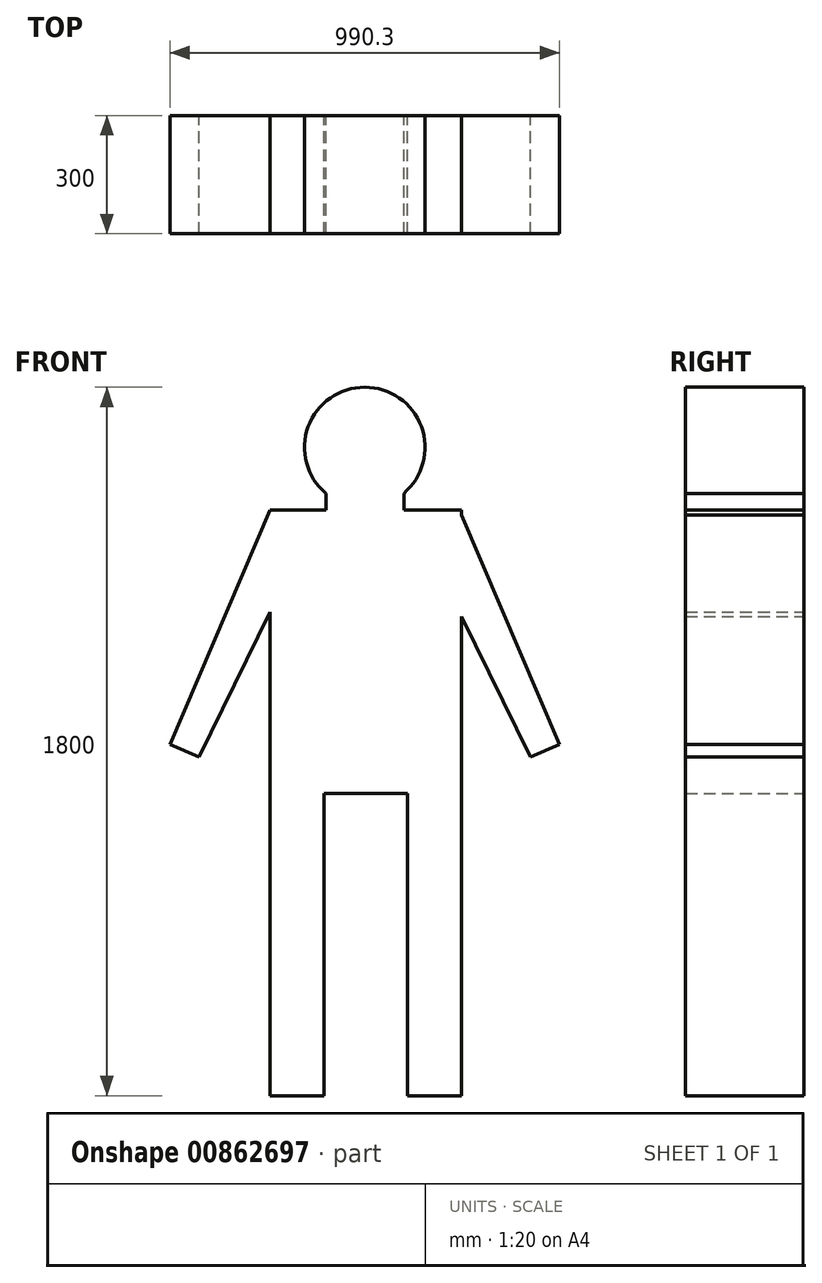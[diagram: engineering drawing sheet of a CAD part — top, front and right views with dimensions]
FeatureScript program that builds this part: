
annotation { "Feature Type Name" : "Feature", "Feature Type Description" : "" }
export const myFeature = defineFeature(function(context is Context, id is Id, definition is map)
    precondition{}
    {
        {
            var Q0;
            Q0=qCreatedBy(makeId("Front.planeOp"),FACE);
            var sketch = newSketch(context, id + "F0", { "sketchPlane" : qUnion([Q0])});
            skCircle(sketch, "E0", {"center": v(0, 754.64) * mm, "radius": 153.03 * mm});
            skLineSegment(sketch, "E1.bottom", {"start": v(-240.95, 595.77) * mm, "end": v(246.25, 595.77) * mm});
            skLineSegment(sketch, "E1.top", {"start": v(-240.95, -124.45) * mm, "end": v(246.25, -124.45) * mm});
            skLineSegment(sketch, "E1.left", {"start": v(-240.95, 595.77) * mm, "end": v(-240.95, -124.45) * mm});
            skLineSegment(sketch, "E1.right", {"start": v(246.25, 595.77) * mm, "end": v(246.25, -124.45) * mm});
            skLineSegment(sketch, "E2.bottom", {"start": v(-240.95, -124.45) * mm, "end": v(-103.27, -124.45) * mm});
            skLineSegment(sketch, "E2.top", {"start": v(-240.95, -892.33) * mm, "end": v(-103.27, -892.33) * mm});
            skLineSegment(sketch, "E2.left", {"start": v(-240.95, -124.45) * mm, "end": v(-240.95, -892.33) * mm});
            skLineSegment(sketch, "E2.right", {"start": v(-103.27, -124.45) * mm, "end": v(-103.27, -892.33) * mm});
            skLineSegment(sketch, "E3.bottom", {"start": v(108.56, -124.45) * mm, "end": v(246.25, -124.45) * mm});
            skLineSegment(sketch, "E3.top", {"start": v(108.56, -892.33) * mm, "end": v(246.25, -892.33) * mm});
            skLineSegment(sketch, "E3.left", {"start": v(108.56, -124.45) * mm, "end": v(108.56, -892.33) * mm});
            skLineSegment(sketch, "E3.right", {"start": v(246.25, -124.45) * mm, "end": v(246.25, -892.33) * mm});
            skLineSegment(sketch, "E4", {"start": v(-240.95, 595.77) * mm, "end": v(-495.15, 0) * mm});
            skLineSegment(sketch, "E5", {"start": v(-495.15, 0) * mm, "end": v(-421.26, -31.53) * mm});
            skLineSegment(sketch, "E6", {"start": v(-421.26, -31.53) * mm, "end": v(-240.95, 336.28) * mm});
            skLineSegment(sketch, "E7.MirrorCS", {"start": v(421.26, -31.53) * mm, "end": v(240.95, 336.28) * mm});
            skLineSegment(sketch, "E8.MirrorCS", {"start": v(240.95, 595.77) * mm, "end": v(495.15, 0) * mm});
            skLineSegment(sketch, "E9.MirrorCS", {"start": v(495.15, 0) * mm, "end": v(421.26, -31.53) * mm});
            skLineSegment(sketch, "E10", {"start": v(-99.07, 638) * mm, "end": v(-99.07, 595.77) * mm});
            skLineSegment(sketch, "E11.MirrorCS", {"start": v(99.07, 638) * mm, "end": v(99.07, 595.77) * mm});
            skSolve(sketch);
        }
        {
            var Q0;
            Q0 = qSketchRegion(id + "F0", true);
            extrude(context, id + "F1", {"entities" : qUnion([Q0]), "depth" : 300 * mm, "offsetDistance" : 25 * mm});
        }
    });
